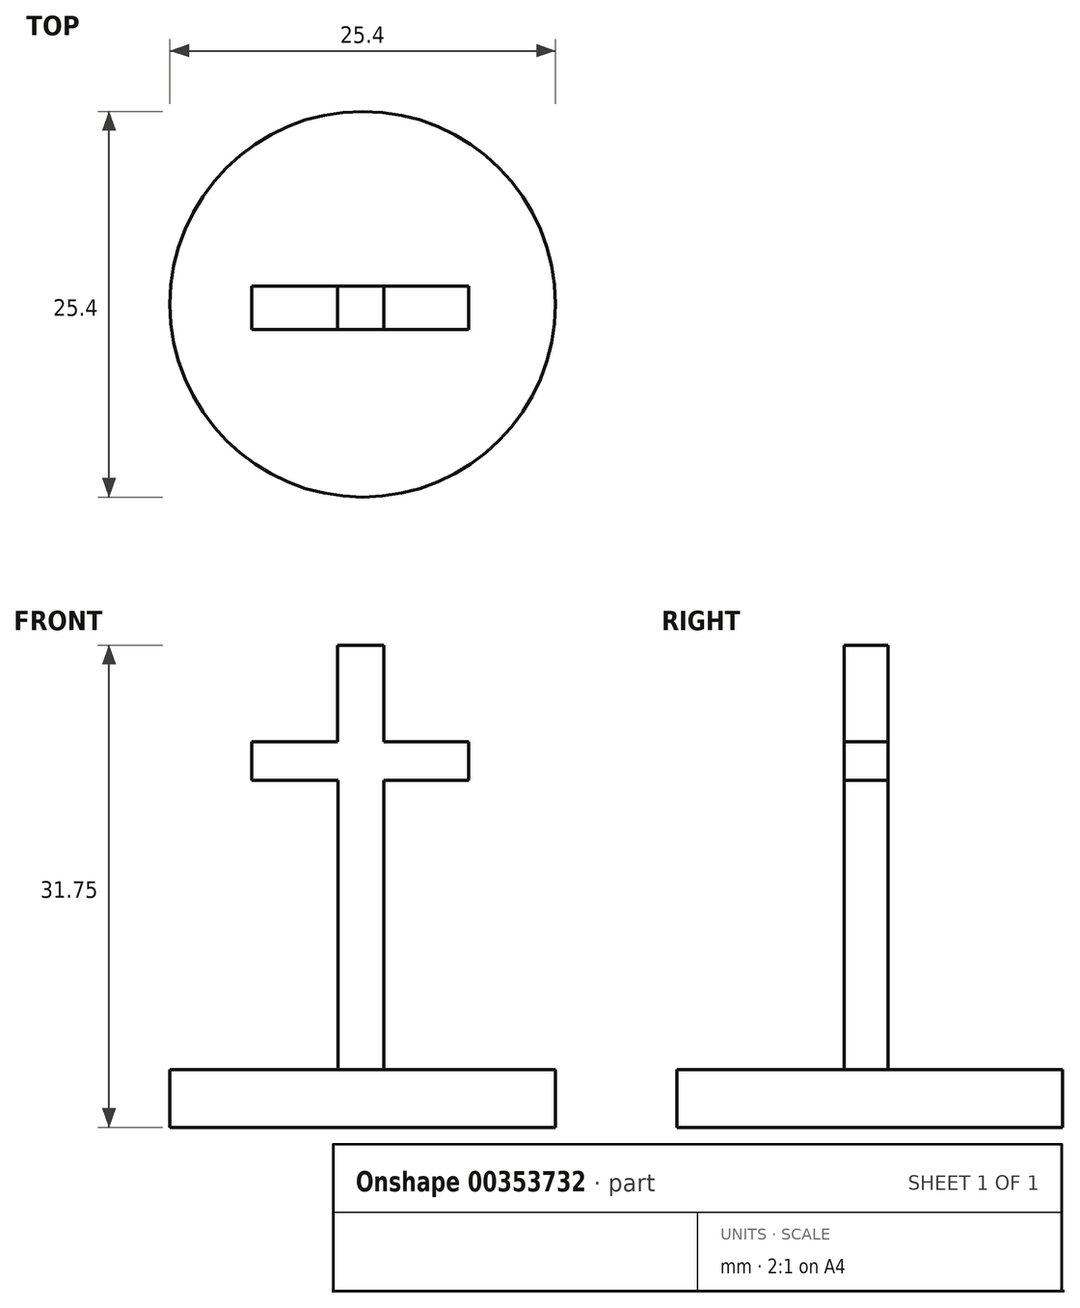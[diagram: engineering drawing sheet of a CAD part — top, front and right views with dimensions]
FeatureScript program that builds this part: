
annotation { "Feature Type Name" : "Feature", "Feature Type Description" : "" }
export const myFeature = defineFeature(function(context is Context, id is Id, definition is map)
    precondition{}
    {
        {
            var Q0;
            Q0=qCreatedBy(makeId("Top.planeOp"),FACE);
            var sketch = newSketch(context, id + "F0", { "sketchPlane" : qUnion([Q0])});
            skCircle(sketch, "E0", {"center": v(0, 0) * mm, "radius": 12.7 * mm});
            skSolve(sketch);
        }
        {
            var Q0;
            Q0=makeQuery(id+"F0.imprint","IMPRINT",FACE,{"disambiguationData":[TD([[makeQuery(id+"F0.imprint","IMPRINT",EDGE,{"derivedFrom":sQuery(id+"F0.wireOp",EDGE,"E0")}),1.0]])]});
            extrude(context, id + "F1", {"entities" : qUnion([Q0]), "depth" : 3.8 * mm});
        }
        {
            var Q0;
            Q0=makeQuery(id+"F1.opExtrude","CAP_FACE",FACE,{"disambiguationData":[OSD([sQuery(id+"F0.wireOp",EDGE,"E0")])],"isStart":false});
            var sketch = newSketch(context, id + "F2", { "sketchPlane" : qUnion([Q0])});
            skLineSegment(sketch, "E1.bottom", {"start": v(-1.64, -1.68) * mm, "end": v(1.4, -1.68) * mm});
            skLineSegment(sketch, "E1.top", {"start": v(-1.64, 1.19) * mm, "end": v(1.4, 1.19) * mm});
            skLineSegment(sketch, "E1.left", {"start": v(-1.64, -1.68) * mm, "end": v(-1.64, 1.19) * mm});
            skLineSegment(sketch, "E1.right", {"start": v(1.4, -1.68) * mm, "end": v(1.4, 1.19) * mm});
            skSolve(sketch);
        }
        {
            var Q0;
            Q0=makeQuery(id+"F2.imprint","IMPRINT",FACE,{"disambiguationData":[TD([[makeQuery(id+"F2.imprint","IMPRINT",EDGE,{"derivedFrom":sQuery(id+"F2.wireOp",EDGE,"E1.bottom")}),1.0]])]});
            extrude(context, id + "F3", {"entities" : qUnion([Q0]), "operationType" : NewBodyOperationType.ADD, "depth" : 19.05 * mm});
        }
        {
            var Q0;
            Q0=makeQuery(id+"F3.opExtrude","CAP_FACE",FACE,{"disambiguationData":[OSD([sQuery(id+"F2.wireOp",EDGE,"E1.bottom"),sQuery(id+"F2.wireOp",EDGE,"E1.top"),sQuery(id+"F2.wireOp",EDGE,"E1.left"),sQuery(id+"F2.wireOp",EDGE,"E1.right")])],"isStart":false});
            var sketch = newSketch(context, id + "F4", { "sketchPlane" : qUnion([Q0])});
            skLineSegment(sketch, "E2.bottom", {"start": v(-7.3, 1.19) * mm, "end": v(6.96, 1.19) * mm});
            skLineSegment(sketch, "E2.top", {"start": v(-7.3, -1.68) * mm, "end": v(6.96, -1.68) * mm});
            skLineSegment(sketch, "E2.left", {"start": v(-7.3, 1.19) * mm, "end": v(-7.3, -1.68) * mm});
            skLineSegment(sketch, "E2.right", {"start": v(6.96, 1.19) * mm, "end": v(6.96, -1.68) * mm});
            skSolve(sketch);
        }
        {
            var Q0;
            {var subQ2=sQuery(id+"F4.wireOp",EDGE,"E2.left");Q0=makeQuery(id+"F4.imprint","IMPRINT",FACE,{"disambiguationData":[TD([[makeQuery(id+"F4.imprint","IMPRINT",EDGE,{"derivedFrom":subQ2}),1.0]])]});}
            var Q1;
            {var subQ1=makeQuery(id+"F3.opExtrude","CAP_EDGE",EDGE,{"disambiguationData":[OSD([sQuery(id+"F2.wireOp",EDGE,"E1.left")])],"isStart":false});Q1=makeQuery(id+"F4.imprint","IMPRINT",FACE,{"disambiguationData":[TD([[makeQuery(id+"F4.imprint","IMPRINT",EDGE,{"derivedFrom":subQ1}),-1.0]])]});}
            var Q2;
            {var subQ2=sQuery(id+"F4.wireOp",EDGE,"E2.right");Q2=makeQuery(id+"F4.imprint","IMPRINT",FACE,{"disambiguationData":[TD([[makeQuery(id+"F4.imprint","IMPRINT",EDGE,{"derivedFrom":subQ2}),-1.0]])]});}
            extrude(context, id + "F5", {"entities" : qUnion([Q0, Q1, Q2]), "operationType" : NewBodyOperationType.ADD, "depth" : 2.54 * mm});
        }
        {
            var Q0;
            Q0=makeQuery(id+"F5.opExtrude","CAP_FACE",FACE,{"disambiguationData":[OSD([sQuery(id+"F4.wireOp",EDGE,"E2.bottom"),sQuery(id+"F4.wireOp",EDGE,"E2.top"),sQuery(id+"F4.wireOp",EDGE,"E2.left"),sQuery(id+"F4.wireOp",EDGE,"E2.right")])],"isStart":false});
            var sketch = newSketch(context, id + "F6", { "sketchPlane" : qUnion([Q0])});
            skLineSegment(sketch, "E3.bottom", {"start": v(-1.65, -1.68) * mm, "end": v(1.38, -1.68) * mm});
            skLineSegment(sketch, "E3.top", {"start": v(-1.65, 1.19) * mm, "end": v(1.38, 1.19) * mm});
            skLineSegment(sketch, "E3.left", {"start": v(-1.65, -1.68) * mm, "end": v(-1.65, 1.19) * mm});
            skLineSegment(sketch, "E3.right", {"start": v(1.38, -1.68) * mm, "end": v(1.38, 1.19) * mm});
            skSolve(sketch);
        }
        {
            var Q0;
            Q0=makeQuery(id+"F6.imprint","IMPRINT",FACE,{"disambiguationData":[TD([[makeQuery(id+"F6.imprint","IMPRINT",EDGE,{"derivedFrom":sQuery(id+"F6.wireOp",EDGE,"E3.bottom")}),1.0]])]});
            extrude(context, id + "F7", {"entities" : qUnion([Q0]), "operationType" : NewBodyOperationType.ADD, "depth" : 6.35 * mm});
        }
    });
